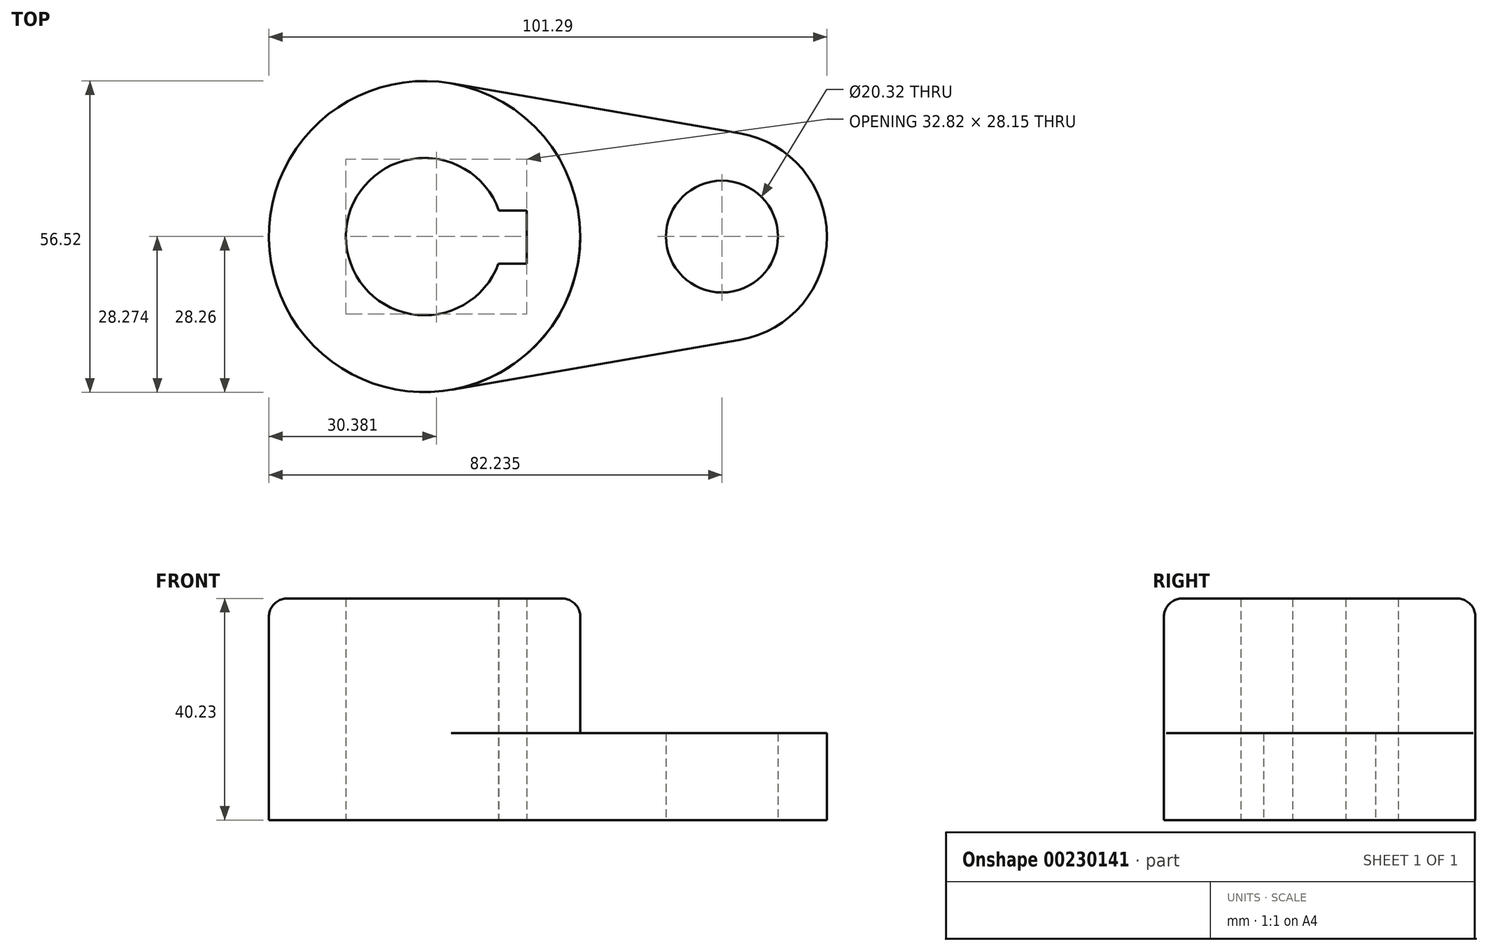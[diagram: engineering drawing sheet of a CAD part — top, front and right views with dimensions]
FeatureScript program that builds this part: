
annotation { "Feature Type Name" : "Feature", "Feature Type Description" : "" }
export const myFeature = defineFeature(function(context is Context, id is Id, definition is map)
    precondition{}
    {
        {
            var Q0;
            Q0=qCreatedBy(makeId("Top.planeOp"),FACE);
            var sketch = newSketch(context, id + "F0", { "sketchPlane" : qUnion([Q0])});
            skCircle(sketch, "E0", {"center": v(0, 0) * mm, "radius": 28.26 * mm});
            skArc(sketch, "E1", {"start": v(57.22, -18.77) * mm, "mid": v(73.03, 0) * mm, "end": v(57.22, 18.77) * mm});
            skLineSegment(sketch, "E2", {"start": v(4.82, 27.84) * mm, "end": v(57.22, 18.77) * mm});
            skLineSegment(sketch, "E3", {"start": v(4.82, -27.84) * mm, "end": v(57.22, -18.77) * mm});
            skArc(sketch, "E4", {"start": v(13.47, 4.75) * mm, "mid": v(-14.29, 0.08) * mm, "end": v(13.42, -4.9) * mm});
            skCircle(sketch, "E5", {"center": v(53.98, 0) * mm, "radius": 10.16 * mm});
            skLineSegment(sketch, "E6.bottom", {"start": v(18.53, -4.9) * mm, "end": v(13.42, -4.9) * mm});
            skLineSegment(sketch, "E6.top", {"start": v(18.53, 4.75) * mm, "end": v(13.47, 4.75) * mm});
            skLineSegment(sketch, "E6.left", {"start": v(18.53, -4.9) * mm, "end": v(18.53, 4.75) * mm});
            skSolve(sketch);
        }
        {
            var Q0;
            Q0=makeQuery(id+"F0.imprint","IMPRINT",FACE,{"disambiguationData":[TD([[makeQuery(id+"F0.imprint","IMPRINT",EDGE,{"derivedFrom":sQuery(id+"F0.wireOp",EDGE,"E4")}),-1.0]])]});
            extrude(context, id + "F1", {"entities" : qUnion([Q0]), "depth" : 40.23 * mm});
        }
        {
            var Q0;
            Q0 = qSketchRegion(id + "F0", true);
            extrude(context, id + "F2", {"entities" : qUnion([Q0]), "operationType" : NewBodyOperationType.ADD, "depth" : 15.77 * mm});
        }
        {
            var Q0;
            Q0=makeQuery(id+"F1.opExtrude","CAP_EDGE",EDGE,{"disambiguationData":[OSD([sQuery(id+"F0.wireOp",EDGE,"E0")])],"isStart":false});
            fillet(context, id + "F3", {"entities" : qUnion([Q0]), "radius" : 3.3 * mm, "tangentPropagation" : true, "allowEdgeOverflow" : false});
        }
    });
